# Revit family: IS_iLife_T5537_BIM_NL
name_source: partatom
category: Plumbing Fixtures
units: mm (PartAtom-declared; Revit-internal decimal feet)

## family parameters
Always vertical = Yes
Cut with Voids When Loaded = No
OmniClass Number = 23.45.05.14.21.11
OmniClass Title = Bath/Shower Units
Part Type = Normal
Room Calculation Point = No
Round Connector Dimension = Use Diameter
Shared = No
Work Plane-Based = No

## types (1)
- T5537EO - IS I.LIFE  WALK-IN PANEL 900 BP BRT/SC
    Accesoires = https://www.idealstandard.nl
    Accessories = https://www.idealstandard.nl
    Afmetingen = 855 x 22 x 855 mm
    AfstandsEenheid = millimeter
    Afwerking = Zilver
    AreaUnits = millimetres
    Artikelnummer = T5537EO
    Artikelomschrijving = I.LIFE  WALK-IN PANEL 900 BP BRT/SC
    Artikelreferentie = I.LIFE  WALK-IN PANEL 900 BP BRT/SC
    AssetType = Fixed
    Auteur = Ideal Standard
    BIMObjectName = IS_IdealStandard_Showerenclosures_i.Life_T5537
    BIMobject category = Shower screens
    BIMobject category code = shower-screens
    BIMobject main category = Sanitary
    BIMobject main category code = sanitary
    BarCode = 8014140515005
    Barcode = 8014140515005
    Beschrijvinggarantie = fabrieksgarantie
    BimObjectNaam = IS_IdealStandard_Showerenclosures_i.Life_T5537
    Brand = Ideal Standard
    Brand url = https://www.idealstandard.nl
    Breedte = 855.604751
    BrutoGewicht = 0
    COBIe Type Category = Plumbing Fixtures
    Color = Bright Silver
    ConnectionType = Plumbing
    Cost = 0 $
    CurrencyUnit = €
    CurrentRevision = 1
    Date of publishing = 15/06/2023
    Default Elevation = 0 mm  [stored 0 ft]
    Description = I.LIFE  WALK-IN PANEL 900 BP BRT/SC
    Diepte = 22 mm
    DurationUnit = years
    DuurEenheid = Jaar
    Edition number = 1
    Eigenschappen = I.LIFE  WALK-IN PANEL 900 BP BRT/SC
    Features = Ideal Standard i.life inlooppaneel met onderprofiel van 900 mm, 8 mm veiligheidsglas transparant Ideal Clean. Aluminium helderzilveren profielen, 1,2 mm dik. Profielafstelling tot 25 mm.
    Finish = Bright Silver
    GTIN code = 8014140515005
    Garantieonderdelen = 2
    Garantieunits = Jaar
    GemaaktOp = 15/06/2023
    HasGrabHandles = No
    Help = https://www.idealstandard.co.uk
    Hoogte = 2001,9
    Hulp = https://www.idealstandard.nl
    IFC Classification = Sanitary Terminal
    IfcExportAs = IfcSanitaryTerminalType
    IfcExportType = SHOWER
    Installatieinstructies = https://www.idealstandard.nl
    InstallationInstructions = https://www.idealstandard.nl
    Kleur = Zilver
    Lengte = 22 mm
    LinearUnits = millimetres
    MainColor = Bright Silver
    MaintenanceInformation = https://www.idealstandard.co.uk
    Manufacturer = Ideal Standard
    Manufacturer name = Ideal Standard
    ManufacturerURL = https://www.idealstandard.nl
    Masterformat 2014 Code = 10 28 19
    Masterformat 2014 Description = Tub and Shower Enclosures
    Mat1 = Glass
    Mat2 = Bright Silver_EO
    Materiaal = Gehard veiligheidsglas
    Material = Toughened safety glass
    Material main = tempered glass
    Merk = Ideal Standard
    Model = T5537EO
    ModelNumber = T5537EO
    ModelReference = I.LIFE  WALK-IN PANEL 900 BP BRT/SC
    NBS Reference Code = 45-35-70/332
    NBS Reference Description = Shower enclosures
    Name = Showerenclosures_i.Life_T5537_IdealStandard
    NettWeight = 48Kg
    Nettogewicht = 48
    NominalDepth = 22 mm
    NominalHeight = 2002 mm
    NominalLength = 22 mm
    NominalWidth = 856 mm
    Normen = Showerenclosures_i.Life_T5537_IdealStandard
    OmniClass Code = 23-31 17 17
    OmniClass Description = Shower Enclosures
    OppervlakteEenheid = millimetre
    Product SKU = T5537
    Product certification = https://www.idealstandard.nl
    Product data url = https://bimobject.com
    Product family = I.life
    Product name = I.LIFE  WALK-IN PANEL 900 BP BRT/SC
    Product url = https://www.idealstandard.nl
    ProductInformation = https://www.idealstandard.nl
    ProductSoort = Douchwanden
    Productinformatie = https://www.idealstandard.nl
    QR code = https://bimobject.com
    Revisie = 1
    Shape = rectangular
    Size = 855 x 22 x 855 mm
    Space = Internal
    SpareParts = https://www.idealstandard.nl
    Technical description = https://www.idealstandard.nl
    Telefoonnummer = 077 355 08 08
    Typeconnectie = loodgieter
    UNSPSC Code = 30181507
    URL = https://www.idealstandard.co.uk
    Uniclass 1.4 Code = L72142
    Uniclass 1.4 Description = Shower Screens, curtains
    Uniclass 2.0 Code = PR -35-06-79
    Uniclass 2.0 Description = Shower Enclosures
    Uniclass2015Beschrijving = Shower Enclosures
    Uniclass2015Code = Pr_40_20_06_79
    Uniclass2015Referentie = Pr_40_20_06_79
    Uniclass2015Title = Shower enclosures
    Uniclass2015Version = v1.22
    Urlproducent = https://www.idealstandard.nl
    ValutaEenheid = Euro
    Versie = 1
    Version = 1
    Vervangingskosten = 0
    VolumeUnits = Litres
    Volumeunits = Liter
    Vorm = rechthoekig
    WRASURL = https://www.wrasapprovals.co.uk
    WarrantyDescription = manufacturer warranty
    WarrantyDurationUnit = Years
    Wisselstukken = https://www.idealstandard.nl
    Youtube clip = https://www.youtube.com

note: [stored X ft] marks values corroborated as IEEE doubles in the binary element streams (Revit-internal decimal feet)

## geometry (parser evidence)
native form markers: Blend x4
no freeform markers — native parametric forms only
